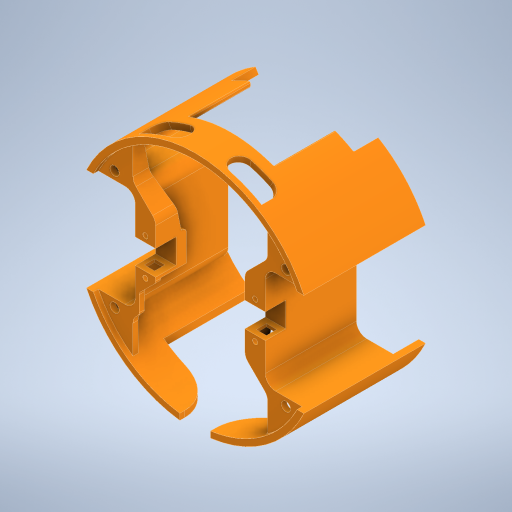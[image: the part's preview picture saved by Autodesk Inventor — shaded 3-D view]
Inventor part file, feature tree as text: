
AUTODESK INVENTOR PART (.ipt)
format: ipt  version: 2023.1 (Build 271208000, 208)  size: 951,808 bytes
history: native  units: mm
features: extrude x17, sketch x13, projected_geometry x11, fillet x7, chamfer x4, other x1
ambient origin geometry x8: Origin, YZ Plane, XZ Plane, XY Plane, X Axis, Y Axis, Z Axis, Center Point
bodies: Body1 (feature_tree)
feature tree (53):
  other  "Sólido1"
  extrude  "Extrusión1"  Depth=3.0mm
  extrude  "Extrusión2"  Depth=18.0mm
  extrude  "Extrusión3"  Depth=15.0mm
  fillet  "Empalme12"  Radius=15.0mm
  extrude  "Extrusión20"  Depth=60.0mm
  extrude  "Extrusión21"  Depth=7.0mm TaperAngle=0.0deg
  sketch  "Boceto16"  dims[d3=50.0mm d4=18.0mm]
  extrude  "Extrusión22"  Depth=5.0mm
  chamfer  "Chaflán3"  [1 undecoded]
  chamfer  "Chaflán4"  Distance=10.0mm
  extrude  "Extrusión24"  Depth=15.0mm
  extrude  "Extrusión25"  Depth=15.0mm
  sketch  "Boceto19"  dims[d13=2.5mm d14=0.0mm d15=7.0mm d16=0.0mm]
  extrude  "Extrusión26"  Depth=15.0mm
  extrude  "Extrusión28"  Depth=15.0mm
  extrude  "Extrusión29"  Depth=15.0mm
  sketch  "Boceto23"  dims[d116=110.0mm]
  sketch  "Boceto24"  dims[d117=41.91mm]
  extrude  "Extrusión30"  Depth=15.0mm
  extrude  "Extrusión31"  Depth=15.0mm
  fillet  "Empalme17"  Radius=10.0mm
  fillet  "Empalme18"  Radius=5.0mm
  chamfer  "Chaflán9"  Distance=4.25mm
  chamfer  "Chaflán10"  Distance=4.25mm
  fillet  "Empalme20"  Radius=1.0mm
  extrude  "Extrusión32"  Depth=15.0mm TaperAngle=0.0deg
  extrude  "Extrusión33"  Depth=10.0mm TaperAngle=45.0deg
  extrude  "Extrusión34"  Depth=15.0mm TaperAngle=45.0deg
  fillet  "Empalme23"  Radius=5.0mm
  fillet  "Empalme24"  Radius=5.0mm
  extrude  "Extrusión35"  Depth=15.0mm TaperAngle=0.0deg
  fillet  "Empalme25"  Radius=5.0mm
  sketch  "Boceto15"  dims[d0=111.5mm d1=3.0mm]
  projected_geometry  "Contorno proyectado16"
  projected_geometry  "Contorno proyectado17"
  projected_geometry  "Contorno proyectado18"
  projected_geometry  "Contorno proyectado19"
  sketch  "Boceto17"  dims[d5=4.5mm d8=9.0mm d9=15.0mm]
  sketch  "Boceto18"  dims[d10=2.5mm d11=0.0mm d12=60.0mm]
  sketch  "Boceto20"  dims[d24=20.0mm d28=5.0mm]
  sketch  "Boceto22"  dims[d76=0.5mm]
  sketch  "Boceto26"  dims[d119=57.92mm]
  projected_geometry  "Contorno proyectado20"
  sketch  "Boceto27"  dims[d120=83.82mm]
  projected_geometry  "Contorno proyectado22"
  projected_geometry  "Contorno proyectado23"
  projected_geometry  "Contorno proyectado24"
  sketch  "Boceto28"  dims[d121=26.04mm]
  projected_geometry  "Contorno proyectado25"
  sketch  "Boceto29"  dims[d131=1.079663mm d132=0.0mm d133=10.0mm d134=2.5mm d135=18.0mm d136=12.15mm d137=18.0mm d138=1.5mm d139=1.5mm d140=5.0mm d141=10.0mm d142=0.0mm d151=5.0mm d152=0.0mm d154=4.25mm d155=4.25mm d156=1.0mm d157=3.0mm d158=0.0mm d159=10.0mm d160=15.0mm d161=45.0deg d162=7.0mm d163=35.0mm d164=45.0deg d180=5.0mm d181=5.0mm d182=1.0mm d183=0.0mm d184=5.0mm d185=5.0mm d186=10.0mm d187=0.0mm d188=4.25mm d189=5.0mm d190=5.0mm d191=20.0mm d192=5.0mm d193=0.0mm d194=0.0mm d197=50.0mm d198=0.0mm d199=42.0mm d200=0.0mm d201=1.0mm d202=1.0mm d203=35.0mm d204=0.0mm d205=1.0mm d206=1.0mm d207=10.0mm d208=0.0mm d209=2.0mm d210=1.0mm d211=2.0mm d212=2.0mm d213=7.0mm d214=35.0mm d215=45.0deg d217=7.0mm d218=35.0mm d219=45.0deg d220=3.5mm d225=20.0mm d226=10.0mm d227=0.0mm d228=35.0mm d229=0.0mm d230=46.0mm d231=41.0mm d232=30.0mm d233=0.0mm d234=0.5mm d235=5.0mm d236=1.0mm d237=0.0mm d238=15.0mm d42=0.5mm d43=0.872665mm d44=0.5mm d45=0.872665mm d125=0.5mm d126=0.872665mm d127=0.5mm d128=0.872665mm]
  projected_geometry  "Contorno proyectado26"
  projected_geometry  "Contorno proyectado27"
note: 1 required parameter value undecoded (feature->parameter linkage not recoverable at this tier; creation-order binding heuristic only, values carry confidence <= 0.55)
